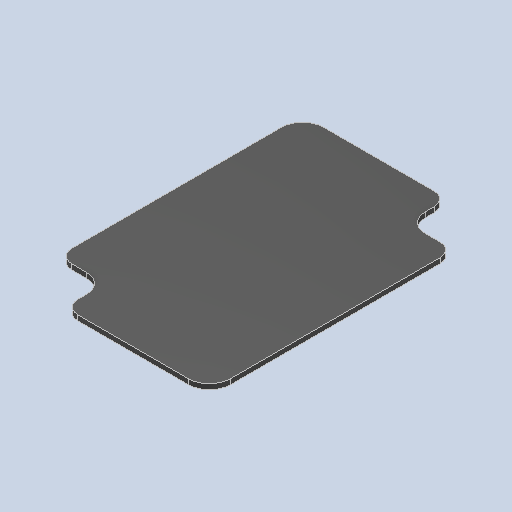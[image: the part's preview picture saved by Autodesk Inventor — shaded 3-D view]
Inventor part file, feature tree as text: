
AUTODESK INVENTOR PART (.ipt)
format: ipt  version: 2022.3 (Build 263350000, 350)  size: 94,208 bytes
history: native  units: in
note: dims shown in document units (in); Inventor stores cm internally (conversion verified against a paired STEP export)
features: fillet x1
ambient origin geometry x8: Origin, YZ Plane, XZ Plane, XY Plane, X Axis, Y Axis, Z Axis, Center Point
bodies: Solid1 (feature_tree)
feature tree (1):
  fillet  "Fillet3"  [1 undecoded]
note: 1 required parameter value undecoded (feature->parameter linkage not recoverable at this tier; creation-order binding heuristic only, values carry confidence <= 0.55)
